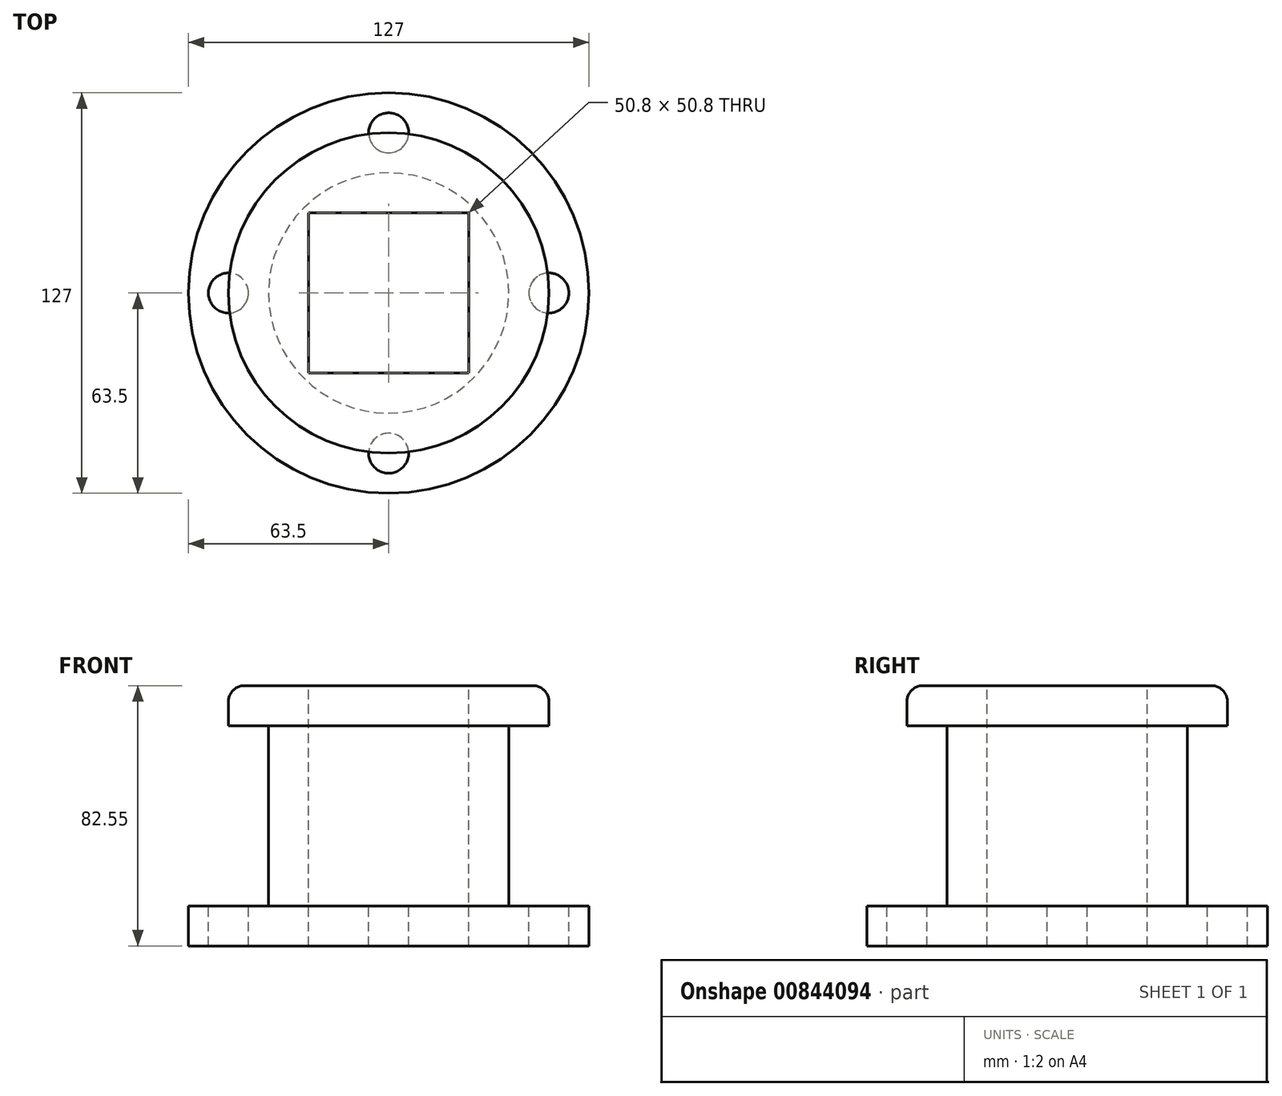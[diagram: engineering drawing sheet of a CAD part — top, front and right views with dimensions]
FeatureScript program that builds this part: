
annotation { "Feature Type Name" : "Feature", "Feature Type Description" : "" }
export const myFeature = defineFeature(function(context is Context, id is Id, definition is map)
    precondition{}
    {
        {
            var Q0;
            Q0=qCreatedBy(makeId("Top.planeOp"),FACE);
            var sketch = newSketch(context, id + "F0", { "sketchPlane" : qUnion([Q0])});
            skCircle(sketch, "E0", {"center": v(0, 0) * mm, "radius": 63.5 * mm});
            skSolve(sketch);
        }
        {
            var Q0;
            Q0 = qSketchRegion(id + "F0", true);
            extrude(context, id + "F1", {"entities" : qUnion([Q0]), "depth" : 12.7 * mm, "offsetDistance" : 25.4 * mm});
        }
        {
            var Q0;
            Q0=makeQuery(id+"F1.opExtrude","CAP_FACE",FACE,{"disambiguationData":[OSD([sQuery(id+"F0.wireOp",EDGE,"E0")])],"isStart":false});
            var sketch = newSketch(context, id + "F2", { "sketchPlane" : qUnion([Q0])});
            skCircle(sketch, "E1", {"center": v(0, 0) * mm, "radius": 38.1 * mm});
            skSolve(sketch);
        }
        {
            var Q0;
            Q0 = qSketchRegion(id + "F2", true);
            extrude(context, id + "F3", {"entities" : qUnion([Q0]), "operationType" : NewBodyOperationType.ADD, "depth" : 57.15 * mm, "offsetDistance" : 25.4 * mm});
        }
        {
            var Q0;
            Q0=qCreatedBy(makeId("Top.planeOp"),FACE);
            var sketch = newSketch(context, id + "F4", { "sketchPlane" : qUnion([Q0])});
            skCircle(sketch, "E2", {"center": v(0, 0) * mm, "radius": 50.8 * mm});
            skSolve(sketch);
        }
        {
            var Q0;
            Q0=makeQuery(id+"F3.opExtrude","CAP_FACE",FACE,{"disambiguationData":[OSD([sQuery(id+"F2.wireOp",EDGE,"E1")])],"isStart":false});
            var sketch = newSketch(context, id + "F5", { "sketchPlane" : qUnion([Q0])});
            skCircle(sketch, "E3", {"center": v(0, 0) * mm, "radius": 50.8 * mm});
            skSolve(sketch);
        }
        {
            var Q0;
            Q0 = qSketchRegion(id + "F5", true);
            extrude(context, id + "F6", {"entities" : qUnion([Q0]), "operationType" : NewBodyOperationType.ADD, "depth" : 12.7 * mm, "offsetDistance" : 25.4 * mm});
        }
        {
            var Q0;
            Q0=makeQuery(id+"F1.opExtrude","CAP_FACE",FACE,{"disambiguationData":[OSD([sQuery(id+"F0.wireOp",EDGE,"E0")])],"isStart":false});
            var sketch = newSketch(context, id + "F7", { "sketchPlane" : qUnion([Q0])});
            skCircle(sketch, "E4", {"center": v(0, 50.8) * mm, "radius": 6.35 * mm});
            skCircle(sketch, "E5", {"center": v(-50.8, 0) * mm, "radius": 6.35 * mm});
            skCircle(sketch, "E6", {"center": v(50.8, 0) * mm, "radius": 6.35 * mm});
            skCircle(sketch, "E7", {"center": v(0, -50.8) * mm, "radius": 6.35 * mm});
            skSolve(sketch);
        }
        {
            var Q0;
            Q0 = qSketchRegion(id + "F7", true);
            extrude(context, id + "F8", {"entities" : qUnion([Q0]), "operationType" : NewBodyOperationType.REMOVE, "depth" : 12.7 * mm, "offsetDistance" : 25.4 * mm});
        }
        {
            var Q0;
            Q0=makeQuery(id+"F1.opExtrude","CAP_FACE",FACE,{"disambiguationData":[OSD([sQuery(id+"F0.wireOp",EDGE,"E0")])],"isStart":false});
            var sketch = newSketch(context, id + "F9", { "sketchPlane" : qUnion([Q0])});
            skCircle(sketch, "E8", {"center": v(0, 50.8) * mm, "radius": 6.35 * mm});
            skSolve(sketch);
        }
        {
            var Q0;
            Q0 = qSketchRegion(id + "F9", true);
            extrude(context, id + "F10", {"entities" : qUnion([Q0]), "operationType" : NewBodyOperationType.REMOVE, "oppositeDirection" : true, "depth" : 12.7 * mm, "offsetDistance" : 25.4 * mm});
        }
        {
            var Q0;
            Q0=makeQuery(id+"F1.opExtrude","CAP_FACE",FACE,{"disambiguationData":[OSD([sQuery(id+"F0.wireOp",EDGE,"E0")])],"isStart":false});
            var sketch = newSketch(context, id + "F11", { "sketchPlane" : qUnion([Q0])});
            skCircle(sketch, "E9", {"center": v(-50.8, 0) * mm, "radius": 6.35 * mm});
            skSolve(sketch);
        }
        {
            var Q0;
            Q0 = qSketchRegion(id + "F11", true);
            extrude(context, id + "F12", {"entities" : qUnion([Q0]), "operationType" : NewBodyOperationType.REMOVE, "oppositeDirection" : true, "depth" : 12.7 * mm, "offsetDistance" : 25.4 * mm});
        }
        {
            var Q0;
            Q0=makeQuery(id+"F1.opExtrude","CAP_FACE",FACE,{"disambiguationData":[OSD([sQuery(id+"F0.wireOp",EDGE,"E0")])],"isStart":false});
            var sketch = newSketch(context, id + "F13", { "sketchPlane" : qUnion([Q0])});
            skCircle(sketch, "E10", {"center": v(0, -50.8) * mm, "radius": 6.35 * mm});
            skSolve(sketch);
        }
        {
            var Q0;
            Q0 = qSketchRegion(id + "F13", true);
            extrude(context, id + "F14", {"entities" : qUnion([Q0]), "operationType" : NewBodyOperationType.REMOVE, "oppositeDirection" : true, "depth" : 25.4 * mm, "offsetDistance" : 25.4 * mm});
        }
        {
            var Q0;
            Q0=makeQuery(id+"F1.opExtrude","CAP_FACE",FACE,{"disambiguationData":[OSD([sQuery(id+"F0.wireOp",EDGE,"E0")])],"isStart":false});
            var sketch = newSketch(context, id + "F15", { "sketchPlane" : qUnion([Q0])});
            skCircle(sketch, "E11", {"center": v(50.8, 0) * mm, "radius": 6.35 * mm});
            skSolve(sketch);
        }
        {
            var Q0;
            Q0 = qSketchRegion(id + "F15", true);
            extrude(context, id + "F16", {"entities" : qUnion([Q0]), "operationType" : NewBodyOperationType.REMOVE, "oppositeDirection" : true, "depth" : 25.4 * mm, "offsetDistance" : 25.4 * mm});
        }
        {
            var Q0;
            Q0=makeQuery(id+"F6.opExtrude","CAP_FACE",FACE,{"disambiguationData":[OSD([sQuery(id+"F5.wireOp",EDGE,"E3")])],"isStart":false});
            var sketch = newSketch(context, id + "F17", { "sketchPlane" : qUnion([Q0])});
            skSolve(sketch);
        }
        {
            var Q0;
            Q0=makeQuery(id+"F6.opExtrude","CAP_EDGE",EDGE,{"disambiguationData":[OSD([sQuery(id+"F5.wireOp",EDGE,"E3")])],"isStart":false});
            fillet(context, id + "F18", {"entities" : qUnion([Q0]), "radius" : 5.08 * mm, "tangentPropagation" : true, "allowEdgeOverflow" : false});
        }
        {
            var Q0;
            Q0=makeQuery(id+"F17.imprint","IMPRINT",FACE,{"disambiguationData":[TD([[makeQuery(id+"F17.imprint","IMPRINT",EDGE,{"derivedFrom":makeQuery(id+"F6.opExtrude","CAP_EDGE",EDGE,{"disambiguationData":[OSD([sQuery(id+"F5.wireOp",EDGE,"E3")])],"isStart":false})}),1.0]])]});
            var sketch = newSketch(context, id + "F19", { "sketchPlane" : qUnion([Q0])});
            skLineSegment(sketch, "E12.bottom", {"start": v(-25.4, 25.4) * mm, "end": v(25.4, 25.4) * mm});
            skLineSegment(sketch, "E12.top", {"start": v(-25.4, -25.4) * mm, "end": v(25.4, -25.4) * mm});
            skLineSegment(sketch, "E12.left", {"start": v(-25.4, 25.4) * mm, "end": v(-25.4, -25.4) * mm});
            skLineSegment(sketch, "E12.right", {"start": v(25.4, 25.4) * mm, "end": v(25.4, -25.4) * mm});
            skSolve(sketch);
        }
        {
            var Q0;
            Q0 = qSketchRegion(id + "F19", true);
            extrude(context, id + "F20", {"entities" : qUnion([Q0]), "operationType" : NewBodyOperationType.REMOVE, "oppositeDirection" : true, "depth" : 431.8 * mm, "offsetDistance" : 25.4 * mm});
        }
    });
